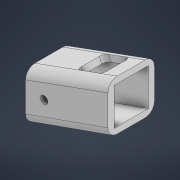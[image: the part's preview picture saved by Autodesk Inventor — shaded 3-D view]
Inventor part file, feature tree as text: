
AUTODESK INVENTOR PART (.ipt)
format: ipt  version: 2021 (Build 250183000, 183)  size: 346,112 bytes
history: native  units: mm
features: sketch x6, extrude x6, fillet x2, plane x1, shell x1
ambient origin geometry x8: Origin, YZ Plane, XZ Plane, XY Plane, X Axis, Y Axis, Z Axis, Center Point
bodies: Volumenkörper1 (feature_tree)
feature tree (16):
  sketch  "Skizze1"  dims[d0=17.434mm d1=110.0mm]
  plane  "Arbeitsebene2"
  extrude  "Extrusion2"  Depth=110.0mm
  extrude  "Extrusion4"  Depth=20.0mm
  extrude  "Extrusion5"  Depth=2.0mm
  shell  "Wandung2"  Thickness=2.0mm
  fillet  "Rundung5"  Radius=3.2mm
  extrude  "Extrusion6"  TaperAngle=0.0deg  [1 undecoded]
  fillet  "Rundung6"  Radius=10.0mm
  extrude  "Extrusion7"  Depth=20.0mm
  extrude  "Extrusion8"  Depth=20.0mm
  sketch  "Skizze3"  dims[d4=20.0mm d5=11.128mm]
  sketch  "Skizze5"  dims[d13=14.4mm d14=14.4mm d15=2.0mm]
  sketch  "Skizze6"  dims[d16=15.0mm d17=7.5mm d18=0.0mm d19=0.0mm d29=3.2mm]
  sketch  "Skizze7"  dims[d31=0.0mm d32=0.0mm d34=10.0mm d35=0.0mm]
  sketch  "Skizze8"  dims[d38=4.706446mm d39=16.495633mm d40=3.490659mm d42=20.0mm d43=0.0mm d44=28.012412mm d45=2.6mm d46=4.0mm d47=7.2mm d48=9.0mm d49=12.0mm d50=12.0mm d51=4.0mm d52=19.0mm d53=3.0mm d54=0.0mm d55=2.0mm d56=3.490659mm d57=3.2mm d58=8.0mm d59=3.0mm d60=0.0mm d61=20.0mm d62=0.0mm]
note: 1 required parameter value undecoded (feature->parameter linkage not recoverable at this tier; creation-order binding heuristic only, values carry confidence <= 0.55)
